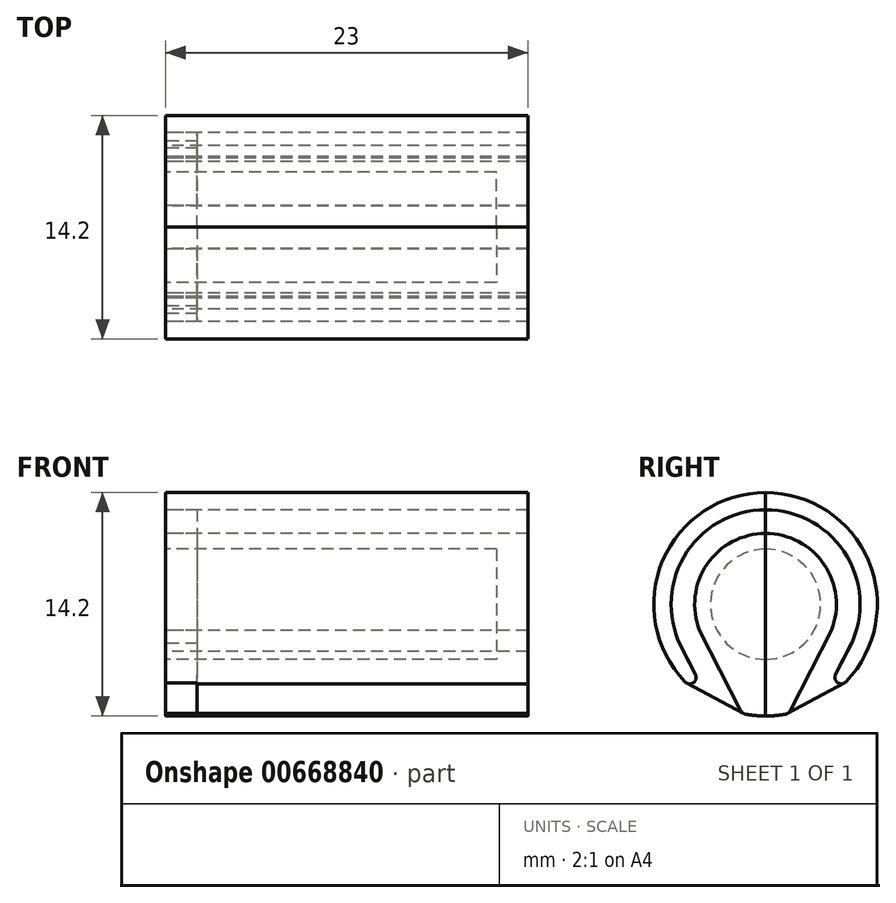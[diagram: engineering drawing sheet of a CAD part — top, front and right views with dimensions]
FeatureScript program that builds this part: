
annotation { "Feature Type Name" : "Feature", "Feature Type Description" : "" }
export const myFeature = defineFeature(function(context is Context, id is Id, definition is map)
    precondition{}
    {
        {
            var Q0;
            Q0=qCreatedBy(makeId("Right.planeOp"),FACE);
            var sketch = newSketch(context, id + "F0", { "sketchPlane" : qUnion([Q0])});
            skArc(sketch, "E0", {"start": v(0, 3.5) * mm, "mid": v(-3.5, 0) * mm, "end": v(0, -3.5) * mm});
            skArc(sketch, "E1", {"start": v(0, 4.5) * mm, "mid": v(-3.72, 2.53) * mm, "end": v(-4.19, -1.65) * mm});
            skArc(sketch, "E2", {"start": v(-1.2, -7) * mm, "mid": v(-0.6, -7.07) * mm, "end": v(0, -7.1) * mm});
            skLineSegment(sketch, "E3", {"start": v(-5.47, -2.48) * mm, "end": v(-4.45, -4.45) * mm});
            skLineSegment(sketch, "E4", {"start": v(0, 7.1) * mm, "end": v(0, 6) * mm});
            skArc(sketch, "E5.trimOffspring", {"start": v(0, 7.1) * mm, "mid": v(-6.53, 2.78) * mm, "end": v(-5.12, -4.92) * mm});
            skArc(sketch, "E6.trimOffspring", {"start": v(0, 6) * mm, "mid": v(-5.2, 3) * mm, "end": v(-5.2, -3) * mm});
            skLineSegment(sketch, "E7.trimOffspring", {"start": v(0, -3.5) * mm, "end": v(0, -7.1) * mm});
            skLineSegment(sketch, "E8.trimOffspring", {"start": v(0, 4.5) * mm, "end": v(0, 3.5) * mm});
            skLineSegment(sketch, "E9", {"start": v(-4.19, -1.65) * mm, "end": v(-1.58, -6.73) * mm});
            skLineSegment(sketch, "E10", {"start": v(-1.2, -7) * mm, "end": v(-1.22, -7) * mm});
            skPoint(sketch, "E11.visualSharp", {"position": v(-3.6, -6.12) * mm});
            skArc(sketch, "E11.filletArc", {"start": v(-5.12, -4.92) * mm, "mid": v(-4.58, -4.97) * mm, "end": v(-4.45, -4.45) * mm});
            skPoint(sketch, "E12.visualSharp", {"position": v(-1.47, -6.95) * mm});
            skArc(sketch, "E12.filletArc", {"start": v(-1.58, -6.73) * mm, "mid": v(-1.44, -6.9) * mm, "end": v(-1.22, -7) * mm});
            skLineSegment(sketch, "E13", {"start": v(-1.36, -6.95) * mm, "end": v(-5.01, -5) * mm});
            skLineSegment(sketch, "E14", {"start": v(0, 6) * mm, "end": v(0, 4.5) * mm});
            skLineSegment(sketch, "E15", {"start": v(0, 3.5) * mm, "end": v(0, -3.5) * mm});
            skSolve(sketch);
        }
        {
            var Q0;
            {var subQ3=sQuery(id+"F0.wireOp",EDGE,"E4");Q0=makeQuery(id+"F0.imprint","IMPRINT",FACE,{"disambiguationData":[TD([[makeQuery(id+"F0.imprint","IMPRINT",EDGE,{"derivedFrom":subQ3}),-1.0]])]});}
            var Q1;
            Q1=makeQuery(id+"F0.imprint","IMPRINT",FACE,{"disambiguationData":[TD([[makeQuery(id+"F0.imprint","IMPRINT",EDGE,{"derivedFrom":sQuery(id+"F0.wireOp",EDGE,"E0")}),-1.0]])]});
            extrude(context, id + "F1", {"entities" : qUnion([Q0, Q1]), "depth" : 23 * mm, "offsetDistance" : 25 * mm});
        }
        {
            var Q0;
            Q0=makeQuery(id+"F0.imprint","IMPRINT",FACE,{"disambiguationData":[TD([[makeQuery(id+"F0.imprint","IMPRINT",EDGE,{"derivedFrom":sQuery(id+"F0.wireOp",EDGE,"E1")}),-1.0]])]});
            extrude(context, id + "F2", {"entities" : qUnion([Q0]), "depth" : 2 * mm, "offsetDistance" : 25 * mm});
        }
        {
            var Q0;
            Q0=makeQuery(id+"F0.imprint","IMPRINT",FACE,{"disambiguationData":[TD([[makeQuery(id+"F0.imprint","IMPRINT",EDGE,{"derivedFrom":sQuery(id+"F0.wireOp",EDGE,"E0")}),1.0]])]});
            extrude(context, id + "F3", {"entities" : qUnion([Q0]), "operationType" : NewBodyOperationType.ADD, "depth" : 23 * mm, "offsetDistance" : 25 * mm});
        }
        {
            var Q0;
            Q0=makeQuery(id+"F0.imprint","IMPRINT",FACE,{"disambiguationData":[TD([[makeQuery(id+"F0.imprint","IMPRINT",EDGE,{"derivedFrom":sQuery(id+"F0.wireOp",EDGE,"E0")}),1.0]])]});
            extrude(context, id + "F4", {"entities" : qUnion([Q0]), "operationType" : NewBodyOperationType.REMOVE, "depth" : 21 * mm, "offsetDistance" : 25 * mm});
        }
        {
            var Q0;
            Q0=makeQuery(id+"F1.opExtrude","SWEPT_BODY",BODY,{"disambiguationData":[OSD([sQuery(id+"F0.wireOp",EDGE,"E0"),sQuery(id+"F0.wireOp",EDGE,"E1"),sQuery(id+"F0.wireOp",EDGE,"E2"),sQuery(id+"F0.wireOp",EDGE,"E7.trimOffspring"),sQuery(id+"F0.wireOp",EDGE,"E8.trimOffspring"),sQuery(id+"F0.wireOp",EDGE,"E9"),sQuery(id+"F0.wireOp",EDGE,"E10"),sQuery(id+"F0.wireOp",EDGE,"E12.filletArc"),sQuery(id+"F0.wireOp",EDGE,"E13")])]});
            var Q1;
            Q1=makeQuery(id+"F1.opExtrude","SWEPT_BODY",BODY,{"disambiguationData":[OSD([sQuery(id+"F0.wireOp",EDGE,"E3"),sQuery(id+"F0.wireOp",EDGE,"E4"),sQuery(id+"F0.wireOp",EDGE,"E5.trimOffspring"),sQuery(id+"F0.wireOp",EDGE,"E6.trimOffspring"),sQuery(id+"F0.wireOp",EDGE,"E11.filletArc")])]});
            var Q2;
            Q2=makeQuery(id+"F2.opExtrude","SWEPT_BODY",BODY,{"disambiguationData":[OSD([sQuery(id+"F0.wireOp",EDGE,"E1"),sQuery(id+"F0.wireOp",EDGE,"E3"),sQuery(id+"F0.wireOp",EDGE,"E6.trimOffspring"),sQuery(id+"F0.wireOp",EDGE,"E9"),sQuery(id+"F0.wireOp",EDGE,"E11.filletArc"),sQuery(id+"F0.wireOp",EDGE,"E12.filletArc"),sQuery(id+"F0.wireOp",EDGE,"E13"),sQuery(id+"F0.wireOp",EDGE,"E14")])]});
            var Q3;
            Q3=qCreatedBy(makeId("Front.planeOp"),FACE);
            mirror(context, id + "F5", {"entities" : qUnion([Q0, Q1, Q2]), "mirrorPlane" : qUnion([Q3])});
        }
    });
